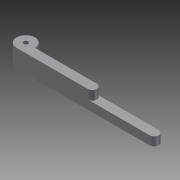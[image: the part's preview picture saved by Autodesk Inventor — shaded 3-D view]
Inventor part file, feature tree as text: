
AUTODESK INVENTOR PART (.ipt)
format: ipt  version: 2011 (Build 150239000, 239)  size: 77,824 bytes
history: native  units: mm
features: other x4, sketch x1
ambient origin geometry x8: Origin, YZ Plane, XZ Plane, XY Plane, X Axis, Y Axis, Z Axis, Center Point
feature tree (5):
  other  "Traba.ipt"
  other  "Sólido1::Traba.ipt"
  sketch  "Boceto1"  dims[d0=10.0mm]
  other  "OperaciónIdentificador1"
  other  "Sólido1"
